# Revit family: Keilhauer_Pact_Bench_120 Corner_77151
name_source: partatom
category: Furniture
revit_build: Autodesk Revit 2017 (Build: 20160225_1515(x64)
units: mm (PartAtom-declared; Revit-internal decimal feet)

## family parameters
Always vertical = Yes
Cut with Voids When Loaded = No
OmniClass Number = 23.40.70.14.64.11
OmniClass Title = Office Furniture
Room Calculation Point = No
Shared = No
Work Plane-Based = No

## types (5) — shared parameters
Assembly Code = E2020200
Catalog = Pact
Manufacturer = Keilhauer, Corp.
Product Documentation Link = http://www.keilhauer.com
URL = http://www.keilhauer.com

## per-type parameters (varying)
| type | Description | Inside | Length | Model | Outside | Type |
| Backless corner | Pact bench backless 120 corner | Yes | 0 mm  [stored 0 ft] | 77140 | No | 1 |
| Back outside corner dividers | Pact bench back 120 outside corner dividers | No | 89 mm  [stored 0.291995 ft] | 77350 | Yes | 5 |
| Back outside corner | Pact bench back 120 outside corner | No | 74.174 mm  [stored 0.243353 ft] | 77151 | Yes | 4 |
| Back inside corner dividers | Pact bench back 120 inside corner dividers | Yes | 74.174 mm  [stored 0.243353 ft] | 77340 | No | 3 |
| Back inside corner | Pact bench back 120 inside corner | Yes | 63.635 mm  [stored 0.208776 ft] | 77141 | No | 2 |

note: [stored X ft] marks values corroborated as IEEE doubles in the binary element streams (Revit-internal decimal feet)

## geometry (parser evidence)
native form markers: Sweep x3
no freeform markers — native parametric forms only
